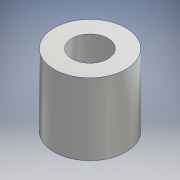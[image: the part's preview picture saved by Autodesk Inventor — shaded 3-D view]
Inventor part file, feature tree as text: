
AUTODESK INVENTOR PART (.ipt)
format: ipt  version: 2016 (Build 200138000, 138)  size: 104,960 bytes
history: native  units: mm
features: other x1, extrude x1, sketch x1
ambient origin geometry x8: Origin, YZ Plane, XZ Plane, XY Plane, X Axis, Y Axis, Z Axis, Center Point
bodies: Body1 (feature_tree)
feature tree (3):
  other  "ソリッド1"
  extrude  "押し出し1"  Depth=4.0mm
  sketch  "スケッチ1"
